# Revit family: 717670001_Fluxómetro Sanitario Palanca
name_source: partatom
category: Plumbing Fixtures
units: mm (PartAtom-declared; Revit-internal decimal feet)

## family parameters
Always vertical = Yes
Cut with Voids When Loaded = No
Part Type = Normal
Room Calculation Point = No
Round Connector Dimension = Use Diameter
Shared = No
Work Plane-Based = No

## types (1)
- 717670001_Fluxómetro Sanitario Palanca
    Alto = 355 mm
    Ancho = 76 mm
    Años de Garantía Producto = 3 años
    Capacidad de flujo = 3,5 Lpf a 50 psi
    Ciclo de vida y desempeño de la descarga = 150.000 ciclos
    Creado por = IDD
    Description = • Fluxómetro manual de accionamiento con palanca.
• Consumo: 3,5 Lpf. - 0,92 Gpf.
• Capacidad de descarga de alta eficiencia.
• Compatible con tazas de entrada superior Corona:
Erie E.S, Adriática E.S y Báltica E.S
    Fecha de creación = 11/08/2020
    Garantía Acabado = 2 años
    Manufacturer = Corona
    Material = Corona_Cromado
    Peso  Bruto = 2.635 g - 5,80 lb
    Peso neto = 2.305 g - 5,08 lb
    Tubería para instalación diámetro de entrada = 1 in NPT
    Tubería para instalación diámetro de salida = Conexión a Racor
a 1-1/2 in NPSM
    URL = https://corona.co

## geometry (parser evidence)
native form markers: Sweep x2
no freeform markers — native parametric forms only
